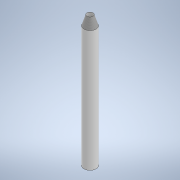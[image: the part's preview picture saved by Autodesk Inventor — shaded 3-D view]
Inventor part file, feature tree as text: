
AUTODESK INVENTOR PART (.ipt)
format: ipt  version: 2022 (Build 260153000, 153)  size: 98,304 bytes
history: native  units: mm
features: revolve x1, thread x1, sketch x1
ambient origin geometry x8: Origin, YZ Plane, XZ Plane, XY Plane, X Axis, Y Axis, Z Axis, Center Point
bodies: Solid1 (feature_tree)
feature tree (3):
  revolve  "Revolution1"  [1 undecoded]
  thread  "Thread1"  [1 undecoded]
  sketch  "Sketch1"  dims[d0=10.0mm d1=200.0mm d2=90.0deg d3=15.765mm d4=0.0mm]
note: 2 required parameter values undecoded (feature->parameter linkage not recoverable at this tier; creation-order binding heuristic only, values carry confidence <= 0.55)